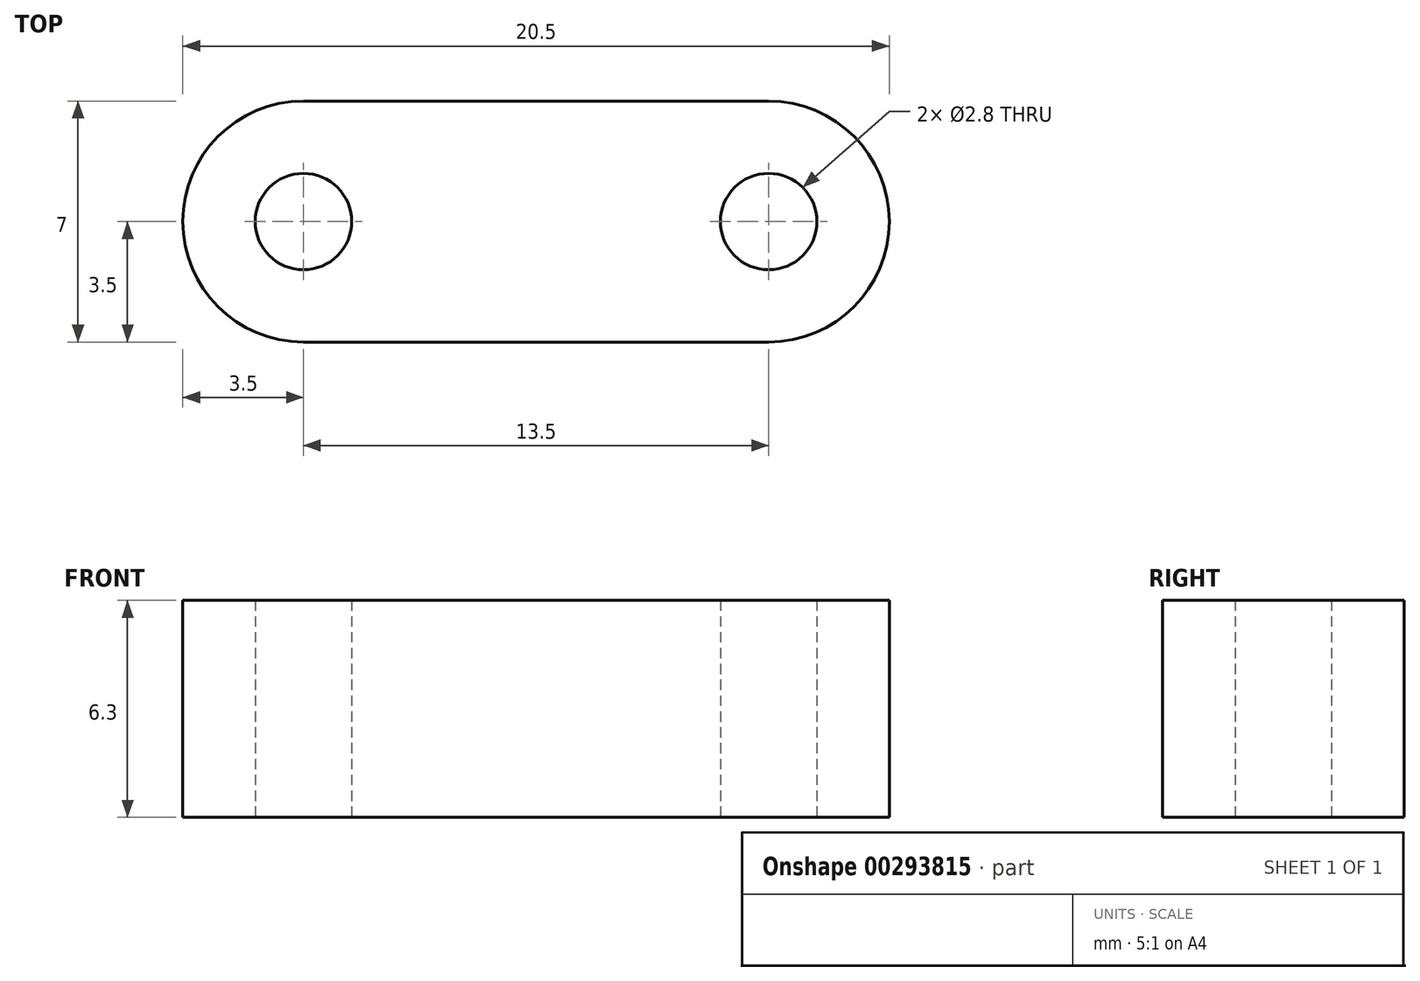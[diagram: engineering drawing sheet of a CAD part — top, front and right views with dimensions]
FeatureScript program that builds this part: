
annotation { "Feature Type Name" : "Feature", "Feature Type Description" : "" }
export const myFeature = defineFeature(function(context is Context, id is Id, definition is map)
    precondition{}
    {
        {
            var Q0;
            Q0=qCreatedBy(makeId("Top.planeOp"),FACE);
            var sketch = newSketch(context, id + "F0", { "sketchPlane" : qUnion([Q0])});
            skCircle(sketch, "E0", {"center": v(0, 0) * mm, "radius": 1.4 * mm});
            skArc(sketch, "E1", {"start": v(0, -3.5) * mm, "mid": v(3.5, 0) * mm, "end": v(0, 3.5) * mm});
            skCircle(sketch, "E2", {"center": v(-13.5, 0) * mm, "radius": 1.4 * mm});
            skArc(sketch, "E3", {"start": v(-13.5, 3.5) * mm, "mid": v(-17, 0) * mm, "end": v(-13.5, -3.5) * mm});
            skLineSegment(sketch, "E4", {"start": v(-13.5, 3.5) * mm, "end": v(0, 3.5) * mm});
            skLineSegment(sketch, "E5", {"start": v(0, -3.5) * mm, "end": v(-13.5, -3.5) * mm});
            skSolve(sketch);
        }
        {
            var Q0;
            Q0 = qSketchRegion(id + "F0", true);
            extrude(context, id + "F1", {"entities" : qUnion([Q0]), "depth" : 6.3 * mm});
        }
    });
